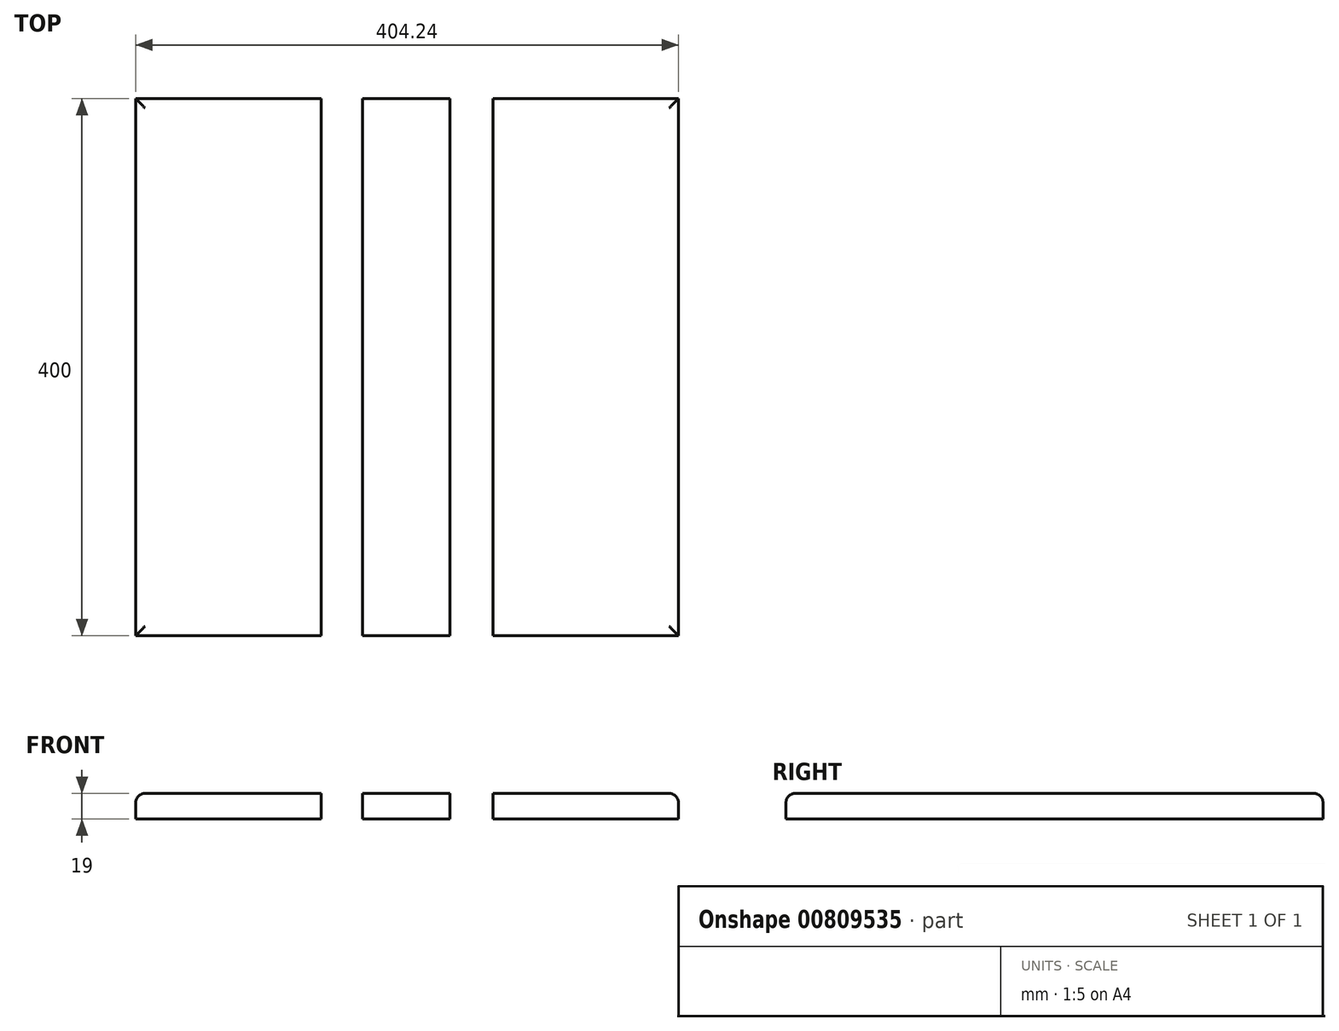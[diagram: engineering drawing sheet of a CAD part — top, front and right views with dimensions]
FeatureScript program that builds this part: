
annotation { "Feature Type Name" : "Feature", "Feature Type Description" : "" }
export const myFeature = defineFeature(function(context is Context, id is Id, definition is map)
    precondition{}
    {
        {
            var Q0;
            Q0=qCreatedBy(makeId("Top.planeOp"),FACE);
            var sketch = newSketch(context, id + "F0", { "sketchPlane" : qUnion([Q0])});
            skLineSegment(sketch, "E0.bottom", {"start": v(-138, 217.86) * mm, "end": v(0, 217.86) * mm});
            skLineSegment(sketch, "E0.top", {"start": v(-138, -182.14) * mm, "end": v(0, -182.14) * mm});
            skLineSegment(sketch, "E0.left", {"start": v(-138, 217.86) * mm, "end": v(-138, -182.14) * mm});
            skLineSegment(sketch, "E0.right", {"start": v(0, 217.86) * mm, "end": v(0, -182.14) * mm});
            skLineSegment(sketch, "E1.bottom", {"start": v(30.89, 217.86) * mm, "end": v(95.89, 217.86) * mm});
            skLineSegment(sketch, "E1.top", {"start": v(30.89, -182.14) * mm, "end": v(95.89, -182.14) * mm});
            skLineSegment(sketch, "E1.left", {"start": v(30.89, 217.86) * mm, "end": v(30.89, -182.14) * mm});
            skLineSegment(sketch, "E1.right", {"start": v(95.89, 217.86) * mm, "end": v(95.89, -182.14) * mm});
            skLineSegment(sketch, "E2.bottom", {"start": v(128.24, 217.86) * mm, "end": v(266.24, 217.86) * mm});
            skLineSegment(sketch, "E2.top", {"start": v(128.24, -182.14) * mm, "end": v(266.24, -182.14) * mm});
            skLineSegment(sketch, "E2.left", {"start": v(128.24, 217.86) * mm, "end": v(128.24, -182.14) * mm});
            skLineSegment(sketch, "E2.right", {"start": v(266.24, 217.86) * mm, "end": v(266.24, -182.14) * mm});
            skSolve(sketch);
        }
        {
            var Q0;
            Q0=makeQuery(id+"F0.imprint","IMPRINT",FACE,{"disambiguationData":[TD([[makeQuery(id+"F0.imprint","IMPRINT",EDGE,{"derivedFrom":sQuery(id+"F0.wireOp",EDGE,"E0.bottom")}),-1.0]])]});
            var Q1;
            Q1=makeQuery(id+"F0.imprint","IMPRINT",FACE,{"disambiguationData":[TD([[makeQuery(id+"F0.imprint","IMPRINT",EDGE,{"derivedFrom":sQuery(id+"F0.wireOp",EDGE,"E1.bottom")}),-1.0]])]});
            var Q2;
            Q2=makeQuery(id+"F0.imprint","IMPRINT",FACE,{"disambiguationData":[TD([[makeQuery(id+"F0.imprint","IMPRINT",EDGE,{"derivedFrom":sQuery(id+"F0.wireOp",EDGE,"E2.bottom")}),-1.0]])]});
            extrude(context, id + "F1", {"entities" : qUnion([Q0, Q1, Q2]), "depth" : 19 * mm, "offsetDistance" : 25 * mm});
        }
        {
            var Q0;
            Q0=makeQuery(id+"F1.opExtrude","CAP_EDGE",EDGE,{"disambiguationData":[OSD([sQuery(id+"F0.wireOp",EDGE,"E0.left")])],"isStart":false});
            var Q1;
            Q1=makeQuery(id+"F1.opExtrude","CAP_EDGE",EDGE,{"disambiguationData":[OSD([sQuery(id+"F0.wireOp",EDGE,"E0.bottom")])],"isStart":false});
            var Q2;
            Q2=makeQuery(id+"F1.opExtrude","CAP_EDGE",EDGE,{"disambiguationData":[OSD([sQuery(id+"F0.wireOp",EDGE,"E1.bottom")])],"isStart":false});
            var Q3;
            Q3=makeQuery(id+"F1.opExtrude","CAP_EDGE",EDGE,{"disambiguationData":[OSD([sQuery(id+"F0.wireOp",EDGE,"E2.bottom")])],"isStart":false});
            var Q4;
            Q4=makeQuery(id+"F1.opExtrude","CAP_EDGE",EDGE,{"disambiguationData":[OSD([sQuery(id+"F0.wireOp",EDGE,"E2.right")])],"isStart":false});
            var Q5;
            Q5=makeQuery(id+"F1.opExtrude","CAP_EDGE",EDGE,{"disambiguationData":[OSD([sQuery(id+"F0.wireOp",EDGE,"E2.top")])],"isStart":false});
            var Q6;
            Q6=makeQuery(id+"F1.opExtrude","CAP_EDGE",EDGE,{"disambiguationData":[OSD([sQuery(id+"F0.wireOp",EDGE,"E1.top")])],"isStart":false});
            var Q7;
            Q7=makeQuery(id+"F1.opExtrude","CAP_EDGE",EDGE,{"disambiguationData":[OSD([sQuery(id+"F0.wireOp",EDGE,"E0.top")])],"isStart":false});
            fillet(context, id + "F2", {"entities" : qUnion([Q0, Q1, Q2, Q3, Q4, Q5, Q6, Q7]), "radius" : 7 * mm, "tangentPropagation" : true, "allowEdgeOverflow" : false});
        }
    });
